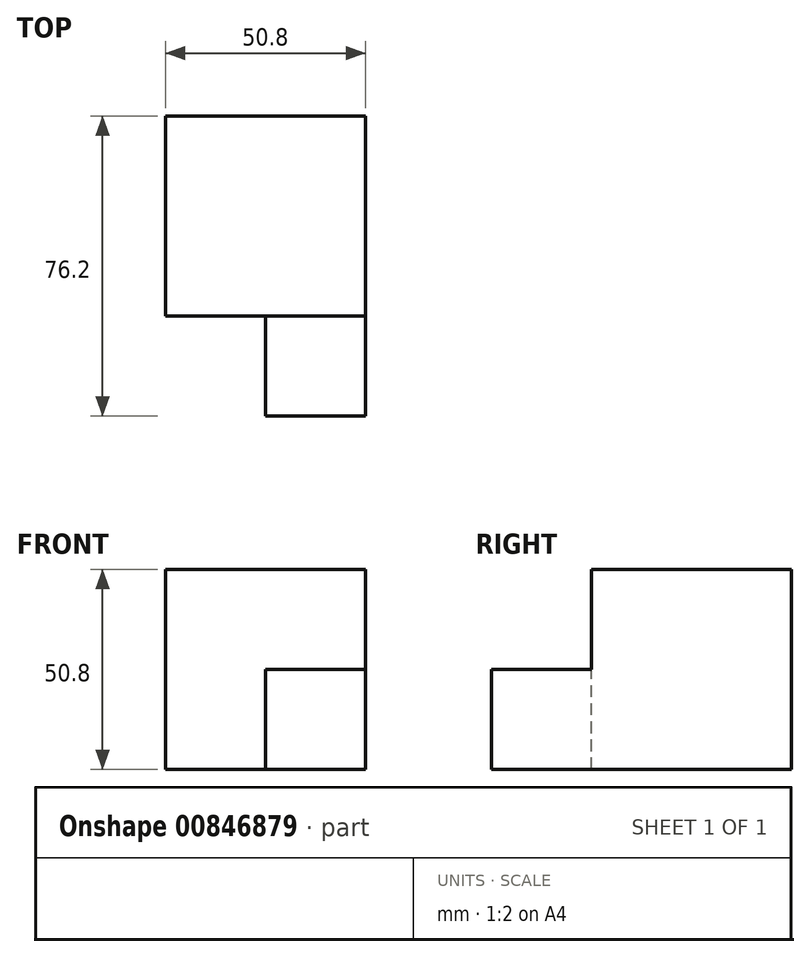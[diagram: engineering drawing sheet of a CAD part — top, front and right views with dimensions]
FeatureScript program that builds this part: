
annotation { "Feature Type Name" : "Feature", "Feature Type Description" : "" }
export const myFeature = defineFeature(function(context is Context, id is Id, definition is map)
    precondition{}
    {
        {
            var Q0;
            Q0=qCreatedBy(makeId("Front.planeOp"),FACE);
            var sketch = newSketch(context, id + "F0", { "sketchPlane" : qUnion([Q0])});
            skLineSegment(sketch, "E0.bottom", {"start": v(0, 0) * mm, "end": v(-50.8, 0) * mm});
            skLineSegment(sketch, "E0.top", {"start": v(0, 50.8) * mm, "end": v(-50.8, 50.8) * mm});
            skLineSegment(sketch, "E0.left", {"start": v(0, 0) * mm, "end": v(0, 50.8) * mm});
            skLineSegment(sketch, "E0.right", {"start": v(-50.8, 0) * mm, "end": v(-50.8, 50.8) * mm});
            skSolve(sketch);
        }
        {
            var Q0;
            Q0=makeQuery(id+"F0.imprint","IMPRINT",FACE,{"disambiguationData":[TD([[makeQuery(id+"F0.imprint","IMPRINT",EDGE,{"derivedFrom":sQuery(id+"F0.wireOp",EDGE,"E0.bottom")}),-1.0]])]});
            extrude(context, id + "F1", {"entities" : qUnion([Q0]), "depth" : 50.8 * mm, "offsetDistance" : 25.4 * mm});
        }
        {
            var Q0;
            Q0=makeQuery(id+"F1.opExtrude","CAP_FACE",FACE,{"disambiguationData":[OSD([sQuery(id+"F0.wireOp",EDGE,"E0.bottom"),sQuery(id+"F0.wireOp",EDGE,"E0.top"),sQuery(id+"F0.wireOp",EDGE,"E0.left"),sQuery(id+"F0.wireOp",EDGE,"E0.right")])],"isStart":false});
            var sketch = newSketch(context, id + "F2", { "sketchPlane" : qUnion([Q0])});
            skLineSegment(sketch, "E1.bottom", {"start": v(-25.4, 0) * mm, "end": v(0, 0) * mm});
            skLineSegment(sketch, "E1.top", {"start": v(-25.4, 25.4) * mm, "end": v(0, 25.4) * mm});
            skLineSegment(sketch, "E1.left", {"start": v(-25.4, 0) * mm, "end": v(-25.4, 25.4) * mm});
            skLineSegment(sketch, "E1.right", {"start": v(0, 0) * mm, "end": v(0, 25.4) * mm});
            skSolve(sketch);
        }
        {
            var Q0;
            Q0=qSketchRegion(id+"F2",true);
            extrude(context, id + "F3", {"entities" : qUnion([Q0]), "operationType" : NewBodyOperationType.ADD, "depth" : 25.4 * mm, "offsetDistance" : 25.4 * mm});
        }
    });
